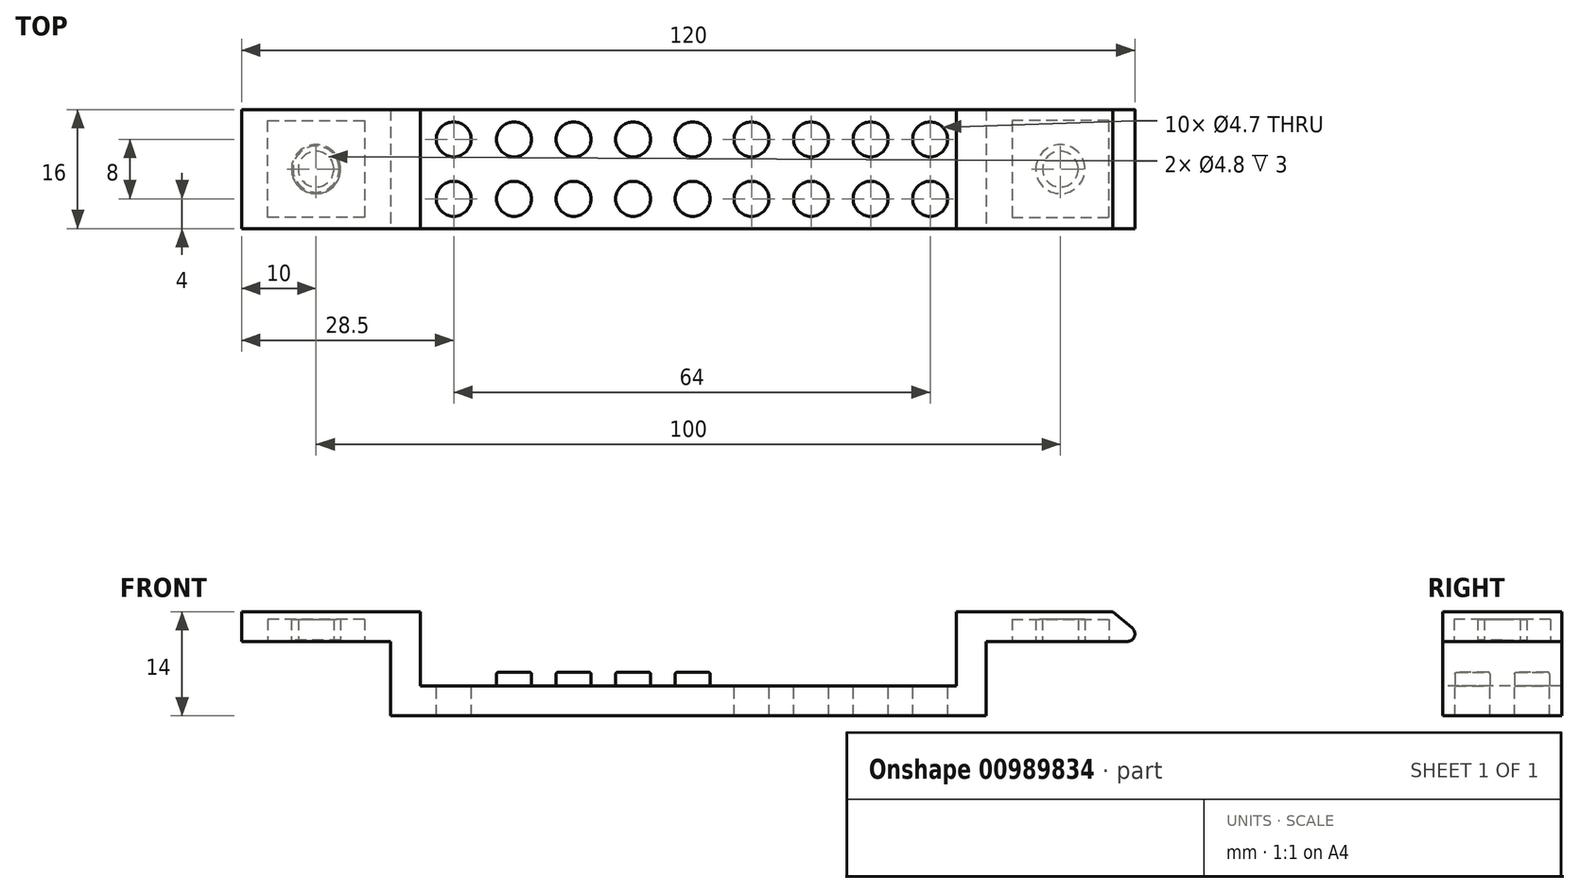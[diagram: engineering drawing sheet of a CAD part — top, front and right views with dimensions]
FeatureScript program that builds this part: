
annotation { "Feature Type Name" : "Feature", "Feature Type Description" : "" }
export const myFeature = defineFeature(function(context is Context, id is Id, definition is map)
    precondition{}
    {
        {
            var Q0;
            Q0=qCreatedBy(makeId("Front.planeOp"),FACE);
            var sketch = newSketch(context, id + "F0", { "sketchPlane" : qUnion([Q0])});
            skLineSegment(sketch, "E0", {"start": v(0, 0) * mm, "end": v(-40, 0) * mm});
            skLineSegment(sketch, "E1", {"start": v(-40, 0) * mm, "end": v(-40, 10) * mm});
            skLineSegment(sketch, "E2", {"start": v(-40, 10) * mm, "end": v(-60, 10) * mm});
            skLineSegment(sketch, "E3.0", {"start": v(-36, 14) * mm, "end": v(-60, 14) * mm});
            skLineSegment(sketch, "E3.1", {"start": v(-36, 4) * mm, "end": v(-36, 14) * mm});
            skLineSegment(sketch, "E3.2", {"start": v(0, 4) * mm, "end": v(-36, 4) * mm});
            skLineSegment(sketch, "E4", {"start": v(-60, 14) * mm, "end": v(-60, 10) * mm});
            skLineSegment(sketch, "E5", {"start": v(0, 4) * mm, "end": v(0, 0) * mm});
            skCircle(sketch, "E6", {"center": v(-50, 6) * mm, "radius": 10 * mm, "construction": true});
            skPoint(sketch, "E6.centerSnap0", {"position": v(-50, 10) * mm});
            skCircle(sketch, "E7", {"center": v(-50, 6) * mm, "radius": 12 * mm, "construction": true});
            skSolve(sketch);
        }
        {
            var Q0;
            Q0=makeQuery(id+"F0.imprint","IMPRINT",FACE,{"disambiguationData":[TD([[makeQuery(id+"F0.imprint","IMPRINT",EDGE,{"derivedFrom":sQuery(id+"F0.wireOp",EDGE,"E0")}),-1.0]])]});
            extrude(context, id + "F1", {"entities" : qUnion([Q0]), "oppositeDirection" : true, "depth" : 16 * mm, "offsetDistance" : 25 * mm});
        }
        {
            var Q0;
            Q0=makeQuery(id+"F1.opExtrude","SWEPT_FACE",FACE,{"disambiguationData":[OSD([sQuery(id+"F0.wireOp",EDGE,"E2")])]});
            var sketch = newSketch(context, id + "F2", { "sketchPlane" : qUnion([Q0])});
            skLineSegment(sketch, "E8", {"start": v(-43.5, -1.5) * mm, "end": v(-56.5, -1.5) * mm});
            skLineSegment(sketch, "E9", {"start": v(-56.5, -1.5) * mm, "end": v(-56.5, -14.5) * mm});
            skLineSegment(sketch, "E10", {"start": v(-56.5, -14.5) * mm, "end": v(-43.5, -14.5) * mm});
            skLineSegment(sketch, "E11", {"start": v(-43.5, -14.5) * mm, "end": v(-43.5, -1.5) * mm});
            skCircle(sketch, "E12.0", {"center": v(-50, -8) * mm, "radius": 2.4 * mm});
            skCircle(sketch, "E13.0", {"center": v(-50, -8) * mm, "radius": 3.3 * mm});
            skLineSegment(sketch, "E14.0", {"start": v(-42, 0) * mm, "end": v(-42, -16) * mm, "construction": true});
            skLineSegment(sketch, "E14.1", {"start": v(-42, 0) * mm, "end": v(-58, 0) * mm, "construction": true});
            skLineSegment(sketch, "E14.2", {"start": v(-58, 0) * mm, "end": v(-58, -16) * mm, "construction": true});
            skLineSegment(sketch, "E14.3", {"start": v(-42, -16) * mm, "end": v(-58, -16) * mm, "construction": true});
            skSolve(sketch);
        }
        {
            var Q0;
            Q0=makeQuery(id+"F2.imprint","IMPRINT",FACE,{"disambiguationData":[TD([[makeQuery(id+"F2.imprint","IMPRINT",EDGE,{"derivedFrom":sQuery(id+"F2.wireOp",EDGE,"E8")}),1.0]])]});
            var Q1;
            Q1=makeQuery(id+"F2.imprint","IMPRINT",FACE,{"disambiguationData":[TD([[makeQuery(id+"F2.imprint","IMPRINT",EDGE,{"derivedFrom":sQuery(id+"F2.wireOp",EDGE,"50b0818d-48c9-435e-a0db-fd159936b803.0")}),1.0]])]});
            var Q2;
            Q2=makeQuery(id+"F2.imprint","IMPRINT",FACE,{"disambiguationData":[TD([[makeQuery(id+"F2.imprint","IMPRINT",EDGE,{"derivedFrom":sQuery(id+"F2.wireOp",EDGE,"E12.0")}),1.0]])]});
            var Q3;
            Q3=makeQuery(id+"F2.imprint","IMPRINT",FACE,{"disambiguationData":[TD([[makeQuery(id+"F2.imprint","IMPRINT",EDGE,{"derivedFrom":sQuery(id+"F2.wireOp",EDGE,"9362b03a-9ce0-4955-ab87-d27d4ad72b78.0")}),1.0]])]});
            extrude(context, id + "F3", {"entities" : qUnion([Q0, Q1, Q2, Q3]), "operationType" : NewBodyOperationType.REMOVE, "oppositeDirection" : true, "depth" : 3 * mm, "offsetDistance" : 25 * mm});
        }
        {
            var Q0;
            Q0=makeQuery(id+"F1.opExtrude","SWEPT_BODY",BODY,{"disambiguationData":[OSD([sQuery(id+"F0.wireOp",EDGE,"E0"),sQuery(id+"F0.wireOp",EDGE,"E1"),sQuery(id+"F0.wireOp",EDGE,"E2"),sQuery(id+"F0.wireOp",EDGE,"E3.0"),sQuery(id+"F0.wireOp",EDGE,"E3.1"),sQuery(id+"F0.wireOp",EDGE,"E3.2"),sQuery(id+"F0.wireOp",EDGE,"E4"),sQuery(id+"F0.wireOp",EDGE,"E5")])]});
            var Q1;
            Q1=makeQuery(id+"F1.opExtrude","SWEPT_FACE",FACE,{"disambiguationData":[OSD([sQuery(id+"F0.wireOp",EDGE,"E5")])]});
            mirror(context, id + "F4", {"operationType" : NewBodyOperationType.ADD, "entities" : qUnion([Q0]), "mirrorPlane" : qUnion([Q1])});
        }
        {
            var Q0;
            {var subQ0=makeQuery(id+"F1.opExtrude","SWEPT_FACE",FACE,{"disambiguationData":[OSD([sQuery(id+"F0.wireOp",EDGE,"E3.2")])]});Q0=makeQuery(id+"F4.boolean.opBoolean","MERGE",FACE,{"derivedFrom":[subQ0,makeQuery(id+"F4.opPattern","COPY",FACE,{"derivedFrom":subQ0,"instanceName":"1"})]});}
            var sketch = newSketch(context, id + "F5", { "sketchPlane" : qUnion([Q0])});
            skLineSegment(sketch, "E15.0", {"start": v(-27.3, 0) * mm, "end": v(4.7, 0) * mm, "construction": true});
            skLineSegment(sketch, "E15.1", {"start": v(-27.3, 0) * mm, "end": v(-27.3, 16) * mm, "construction": true});
            skLineSegment(sketch, "E15.2", {"start": v(-27.3, 16) * mm, "end": v(4.7, 16) * mm, "construction": true});
            skLineSegment(sketch, "E15.3", {"start": v(4.7, 0) * mm, "end": v(4.7, 16) * mm, "construction": true});
            skCircle(sketch, "E15.4", {"center": v(0.6, 4) * mm, "radius": 2.35 * mm});
            skCircle(sketch, "E15.5", {"center": v(0.6, 12) * mm, "radius": 2.35 * mm});
            skCircle(sketch, "E15.6", {"center": v(-7.4, 12) * mm, "radius": 2.35 * mm});
            skCircle(sketch, "E15.7", {"center": v(-7.4, 4) * mm, "radius": 2.35 * mm});
            skCircle(sketch, "E15.8", {"center": v(-15.4, 4) * mm, "radius": 2.35 * mm});
            skCircle(sketch, "E15.9", {"center": v(-15.4, 12) * mm, "radius": 2.35 * mm});
            skCircle(sketch, "E15.10", {"center": v(-23.4, 12) * mm, "radius": 2.35 * mm});
            skCircle(sketch, "E15.11", {"center": v(-23.4, 4) * mm, "radius": 2.35 * mm});
            skSolve(sketch);
        }
        {
            var Q0;
            Q0=makeQuery(id+"F5.imprint","IMPRINT",FACE,{"disambiguationData":[TD([[makeQuery(id+"F5.imprint","IMPRINT",EDGE,{"derivedFrom":sQuery(id+"F5.wireOp",EDGE,"E15.11")}),1.0]])]});
            var Q1;
            Q1=makeQuery(id+"F5.imprint","IMPRINT",FACE,{"disambiguationData":[TD([[makeQuery(id+"F5.imprint","IMPRINT",EDGE,{"derivedFrom":sQuery(id+"F5.wireOp",EDGE,"E15.10")}),1.0]])]});
            var Q2;
            Q2=makeQuery(id+"F5.imprint","IMPRINT",FACE,{"disambiguationData":[TD([[makeQuery(id+"F5.imprint","IMPRINT",EDGE,{"derivedFrom":sQuery(id+"F5.wireOp",EDGE,"E15.9")}),1.0]])]});
            var Q3;
            Q3=makeQuery(id+"F5.imprint","IMPRINT",FACE,{"disambiguationData":[TD([[makeQuery(id+"F5.imprint","IMPRINT",EDGE,{"derivedFrom":sQuery(id+"F5.wireOp",EDGE,"E15.8")}),1.0]])]});
            var Q4;
            Q4=makeQuery(id+"F5.imprint","IMPRINT",FACE,{"disambiguationData":[TD([[makeQuery(id+"F5.imprint","IMPRINT",EDGE,{"derivedFrom":sQuery(id+"F5.wireOp",EDGE,"E15.7")}),1.0]])]});
            var Q5;
            Q5=makeQuery(id+"F5.imprint","IMPRINT",FACE,{"disambiguationData":[TD([[makeQuery(id+"F5.imprint","IMPRINT",EDGE,{"derivedFrom":sQuery(id+"F5.wireOp",EDGE,"E15.6")}),1.0]])]});
            var Q6;
            Q6=makeQuery(id+"F5.imprint","IMPRINT",FACE,{"disambiguationData":[TD([[makeQuery(id+"F5.imprint","IMPRINT",EDGE,{"derivedFrom":sQuery(id+"F5.wireOp",EDGE,"E15.5")}),1.0]])]});
            var Q7;
            Q7=makeQuery(id+"F5.imprint","IMPRINT",FACE,{"disambiguationData":[TD([[makeQuery(id+"F5.imprint","IMPRINT",EDGE,{"derivedFrom":sQuery(id+"F5.wireOp",EDGE,"E15.4")}),1.0]])]});
            extrude(context, id + "F6", {"entities" : qUnion([Q0, Q1, Q2, Q3, Q4, Q5, Q6, Q7]), "operationType" : NewBodyOperationType.ADD, "depth" : 1.85 * mm, "offsetDistance" : 25 * mm});
        }
        {
            var Q0;
            Q0=makeQuery(id+"F4.opPattern","COPY",EDGE,{"derivedFrom":makeQuery(id+"F1.opExtrude","SWEPT_EDGE",EDGE,{"disambiguationData":[OSD([sQuery(id+"F0.wireOp",EDGE,"E3.0"),sQuery(id+"F0.wireOp",EDGE,"E4")])]}),"instanceName":"1"});
            chamfer(context, id + "F7", {"entities" : qUnion([Q0]), "chamferType" : ChamferType.OFFSET_ANGLE, "width" : 2.5 * mm, "oppositeDirection" : false, "angle" : 50 * degree, "tangentPropagation" : true});
        }
        {
            var Q0;
            Q0=makeQuery(id+"F6.opExtrude","CAP_EDGE",EDGE,{"disambiguationData":[OSD([sQuery(id+"F5.wireOp",EDGE,"E15.11")])],"isStart":false});
            var Q1;
            Q1=makeQuery(id+"F6.opExtrude","CAP_EDGE",EDGE,{"disambiguationData":[OSD([sQuery(id+"F5.wireOp",EDGE,"E15.10")])],"isStart":false});
            var Q2;
            Q2=makeQuery(id+"F6.opExtrude","CAP_EDGE",EDGE,{"disambiguationData":[OSD([sQuery(id+"F5.wireOp",EDGE,"E15.9")])],"isStart":false});
            var Q3;
            Q3=makeQuery(id+"F6.opExtrude","CAP_EDGE",EDGE,{"disambiguationData":[OSD([sQuery(id+"F5.wireOp",EDGE,"E15.8")])],"isStart":false});
            var Q4;
            Q4=makeQuery(id+"F6.opExtrude","CAP_EDGE",EDGE,{"disambiguationData":[OSD([sQuery(id+"F5.wireOp",EDGE,"E15.7")])],"isStart":false});
            var Q5;
            Q5=makeQuery(id+"F6.opExtrude","CAP_EDGE",EDGE,{"disambiguationData":[OSD([sQuery(id+"F5.wireOp",EDGE,"E15.6")])],"isStart":false});
            var Q6;
            Q6=makeQuery(id+"F6.opExtrude","CAP_EDGE",EDGE,{"disambiguationData":[OSD([sQuery(id+"F5.wireOp",EDGE,"E15.5")])],"isStart":false});
            var Q7;
            Q7=makeQuery(id+"F6.opExtrude","CAP_EDGE",EDGE,{"disambiguationData":[OSD([sQuery(id+"F5.wireOp",EDGE,"E15.4")])],"isStart":false});
            fillet(context, id + "F8", {"entities" : qUnion([Q0, Q1, Q2, Q3, Q4, Q5, Q6, Q7]), "radius" : .25 * mm, "tangentPropagation" : true, "allowEdgeOverflow" : false});
        }
        {
            var Q0;
            Q0=makeQuery(id+"F3.boolean.opBoolean","COPY",EDGE,{"derivedFrom":makeQuery(id+"F3.opExtrude","CAP_EDGE",EDGE,{"disambiguationData":[OSD([sQuery(id+"F2.wireOp",EDGE,"E13.0")])],"isStart":true})});
            chamfer(context, id + "F9", {"entities" : qUnion([Q0]), "width" : .2 * mm, "tangentPropagation" : true});
        }
        {
            var Q0;
            {var subQ0=sQuery(id+"F0.wireOp",EDGE,"E4");Q0=makeQuery(id+"F7.opChamfer","BLEND_EDGE",EDGE,{"blendedFrom":[makeQuery(id+"F4.opPattern","COPY",EDGE,{"derivedFrom":makeQuery(id+"F1.opExtrude","SWEPT_EDGE",EDGE,{"disambiguationData":[OSD([sQuery(id+"F0.wireOp",EDGE,"E3.0"),subQ0])]}),"instanceName":"1"}),makeQuery(id+"F4.opPattern","COPY",FACE,{"derivedFrom":makeQuery(id+"F1.opExtrude","SWEPT_FACE",FACE,{"disambiguationData":[OSD([subQ0])]}),"instanceName":"1"})],"blendedInto":[makeQuery(id+"F4.opPattern","COPY",FACE,{"derivedFrom":makeQuery(id+"F1.opExtrude","SWEPT_FACE",FACE,{"disambiguationData":[OSD([subQ0])]}),"instanceName":"1"})]});}
            var Q1;
            Q1=makeQuery(id+"F4.opPattern","COPY",EDGE,{"derivedFrom":makeQuery(id+"F1.opExtrude","SWEPT_EDGE",EDGE,{"disambiguationData":[OSD([sQuery(id+"F0.wireOp",EDGE,"E2"),sQuery(id+"F0.wireOp",EDGE,"E4")])]}),"instanceName":"1"});
            fillet(context, id + "F10", {"entities" : qUnion([Q0, Q1]), "radius" : 1 * mm, "tangentPropagation" : true, "allowEdgeOverflow" : false});
        }
        {
            var Q0;
            {var subQ0=makeQuery(id+"F1.opExtrude","SWEPT_FACE",FACE,{"disambiguationData":[OSD([sQuery(id+"F0.wireOp",EDGE,"E3.2")])]});Q0=makeQuery(id+"F4.boolean.opBoolean","MERGE",FACE,{"derivedFrom":[subQ0,makeQuery(id+"F4.opPattern","COPY",FACE,{"derivedFrom":subQ0,"instanceName":"1"})]});}
            var sketch = newSketch(context, id + "F11", { "sketchPlane" : qUnion([Q0])});
            skCircle(sketch, "E16", {"center": v(-31.5, 12) * mm, "radius": 2.35 * mm});
            skCircle(sketch, "E17.0.1.0", {"center": v(-31.5, 4) * mm, "radius": 2.35 * mm});
            skCircle(sketch, "E18", {"center": v(8.5, 12) * mm, "radius": 2.35 * mm});
            skCircle(sketch, "E19.0.1.0", {"center": v(8.5, 4) * mm, "radius": 2.35 * mm});
            skCircle(sketch, "E19.1.0.0", {"center": v(16.5, 12) * mm, "radius": 2.35 * mm});
            skCircle(sketch, "E19.1.1.0", {"center": v(16.5, 4) * mm, "radius": 2.35 * mm});
            skCircle(sketch, "E19.2.0.0", {"center": v(24.5, 12) * mm, "radius": 2.35 * mm});
            skCircle(sketch, "E19.2.1.0", {"center": v(24.5, 4) * mm, "radius": 2.35 * mm});
            skCircle(sketch, "E19.3.0.0", {"center": v(32.5, 12) * mm, "radius": 2.35 * mm});
            skCircle(sketch, "E19.3.1.0", {"center": v(32.5, 4) * mm, "radius": 2.35 * mm});
            skSolve(sketch);
        }
        {
            var Q0;
            Q0=makeQuery(id+"F11.imprint","IMPRINT",FACE,{"disambiguationData":[TD([[makeQuery(id+"F11.imprint","IMPRINT",EDGE,{"derivedFrom":sQuery(id+"F11.wireOp",EDGE,"E17.0.1.0")}),1.0]])]});
            var Q1;
            Q1=makeQuery(id+"F11.imprint","IMPRINT",FACE,{"disambiguationData":[TD([[makeQuery(id+"F11.imprint","IMPRINT",EDGE,{"derivedFrom":sQuery(id+"F11.wireOp",EDGE,"E16")}),1.0]])]});
            var Q2;
            Q2=makeQuery(id+"F11.imprint","IMPRINT",FACE,{"disambiguationData":[TD([[makeQuery(id+"F11.imprint","IMPRINT",EDGE,{"derivedFrom":sQuery(id+"F11.wireOp",EDGE,"E18")}),1.0]])]});
            var Q3;
            Q3=makeQuery(id+"F11.imprint","IMPRINT",FACE,{"disambiguationData":[TD([[makeQuery(id+"F11.imprint","IMPRINT",EDGE,{"derivedFrom":sQuery(id+"F11.wireOp",EDGE,"E19.0.1.0")}),1.0]])]});
            var Q4;
            Q4=makeQuery(id+"F11.imprint","IMPRINT",FACE,{"disambiguationData":[TD([[makeQuery(id+"F11.imprint","IMPRINT",EDGE,{"derivedFrom":sQuery(id+"F11.wireOp",EDGE,"E19.1.1.0")}),1.0]])]});
            var Q5;
            Q5=makeQuery(id+"F11.imprint","IMPRINT",FACE,{"disambiguationData":[TD([[makeQuery(id+"F11.imprint","IMPRINT",EDGE,{"derivedFrom":sQuery(id+"F11.wireOp",EDGE,"E19.1.0.0")}),1.0]])]});
            var Q6;
            Q6=makeQuery(id+"F11.imprint","IMPRINT",FACE,{"disambiguationData":[TD([[makeQuery(id+"F11.imprint","IMPRINT",EDGE,{"derivedFrom":sQuery(id+"F11.wireOp",EDGE,"E19.2.0.0")}),1.0]])]});
            var Q7;
            Q7=makeQuery(id+"F11.imprint","IMPRINT",FACE,{"disambiguationData":[TD([[makeQuery(id+"F11.imprint","IMPRINT",EDGE,{"derivedFrom":sQuery(id+"F11.wireOp",EDGE,"E19.2.1.0")}),1.0]])]});
            var Q8;
            Q8=makeQuery(id+"F11.imprint","IMPRINT",FACE,{"disambiguationData":[TD([[makeQuery(id+"F11.imprint","IMPRINT",EDGE,{"derivedFrom":sQuery(id+"F11.wireOp",EDGE,"E19.3.1.0")}),1.0]])]});
            var Q9;
            Q9=makeQuery(id+"F11.imprint","IMPRINT",FACE,{"disambiguationData":[TD([[makeQuery(id+"F11.imprint","IMPRINT",EDGE,{"derivedFrom":sQuery(id+"F11.wireOp",EDGE,"E19.3.0.0")}),1.0]])]});
            extrude(context, id + "F12", {"entities" : qUnion([Q0, Q1, Q2, Q3, Q4, Q5, Q6, Q7, Q8, Q9]), "operationType" : NewBodyOperationType.REMOVE, "oppositeDirection" : true, "depth" : 25 * mm, "offsetDistance" : 25 * mm});
        }
    });
